# Revit family: Toilet-Floor_Mount-KOHLER-EIR-K-77796T-1
name_source: partatom
category: Plumbing Fixtures
revit_build: Autodesk Revit 2017 (Build: 20160225_1515(x64)
units: mm (PartAtom-declared; Revit-internal decimal feet)

## family parameters
Cut with Voids When Loaded = No
Host = Face
OmniClass Number = 23.31.19.00
Part Type = Normal
Room Calculation Point = No
Round Connector Dimension = Use Diameter
Shared = No

## types (6) — shared parameters
ADA Compliant = No
Apparent Load = 1800 VA
Assembly Code = D2010100
CW Connection = Yes
Cold Water Inlet = Cold Water Inlet
Date Modified = 06/29/2021
Default Elevation = 0"
Description = EIR INTELLIGENT TOILET
Electrical Connector = Yes
Electrical Note = One dedicated circuit required
Finish = Kohler-Vitreous_China-0-White
Flow Rate = 0 GPM
Flush Rate- GPF = 1.0GPF
Flush Rate- LPF = 3.8LPF
HW Connection = No
Hot Water Inlet = Hot Water Inlet
Length = 27 9/16"
Manufacturer = KOHLER Co.
Master Format 2014 = 22 41 13. 13
Master Format 2014 Name = Residential Water Closets
Material = Vitreous China
Pressure = 0.00 psi
Product Name = Eir
Rough-In = 12"
Seat Included = Yes
URL = http://www.kohler.com.cn
Vent Connection = No
Voltage = 120 V
Waste Connection = Yes
Waste Water Outlet = Waste Water Outlet
WaterSense Certified = No
Width = 16 7/16"

## per-type parameters (varying)
| type | Height | Model | Secondary Finish | Type |
| 0- White | 21 1/2" | K-77796T-0 | Kohler-Plastic-0-White | 1 |
| Sunshine Gold, 0-White | 20 9/16" | K-77796T-SG-0 | Kohler-Plastic-SG-Sunshine_Gold | 2 |
| Exposed Chord With Sunshine Gold, 0- White | 20 9/16" | K-77796T-EXSG-0 | Kohler-Plastic-SG-Sunshine_Gold | 3 |
| Exposed Chord, 0- White | 20 9/16" | K-77796T-EX-0 | Kohler-Plastic-0-White | 4 |
| Cloud Smart Version, 0-White | 20 9/16" | K-77796T-XP-0 | Kohler-Plastic-0-White | 5 |
| Exposed Chord With Cloud Smart Version, 0-White | 20 9/16" | K-77796T-XPEX-0 | Kohler-Plastic-0-White | 6 |

## geometry (parser evidence)
native form markers: Sweep x5
no freeform markers — native parametric forms only
